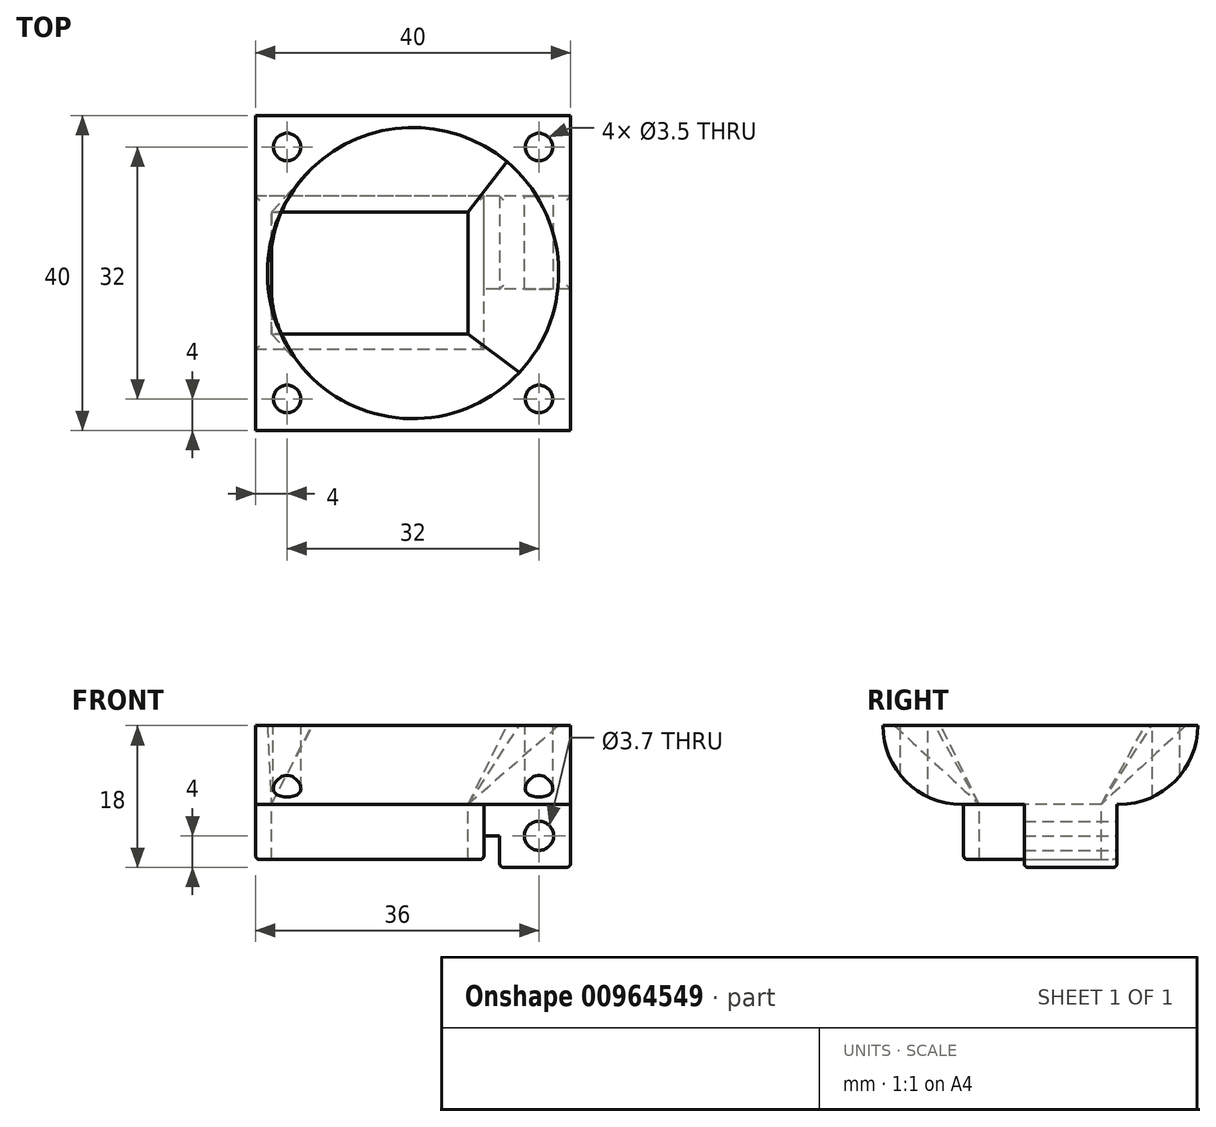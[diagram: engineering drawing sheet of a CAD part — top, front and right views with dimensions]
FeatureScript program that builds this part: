
annotation { "Feature Type Name" : "Feature", "Feature Type Description" : "" }
export const myFeature = defineFeature(function(context is Context, id is Id, definition is map)
    precondition{}
    {
        {
            var Q0;
            Q0=qCreatedBy(makeId("Top.planeOp"),FACE);
            var sketch = newSketch(context, id + "F0", { "sketchPlane" : qUnion([Q0])});
            skLineSegment(sketch, "E0.bottom", {"start": v(20, -9.75) * mm, "end": v(-20, -9.75) * mm});
            skLineSegment(sketch, "E0.top", {"start": v(20, 9.75) * mm, "end": v(-20, 9.75) * mm});
            skLineSegment(sketch, "E0.left", {"start": v(20, -9.75) * mm, "end": v(20, 9.75) * mm});
            skLineSegment(sketch, "E0.right", {"start": v(-20, -9.75) * mm, "end": v(-20, 9.75) * mm});
            skPoint(sketch, "E0.middle", {"position": v(0, 0) * mm});
            skLineSegment(sketch, "E1.bottom", {"start": v(20, -9.75) * mm, "end": v(9, -9.75) * mm});
            skLineSegment(sketch, "E1.top", {"start": v(20, -2.05) * mm, "end": v(9, -2.05) * mm});
            skLineSegment(sketch, "E1.left", {"start": v(20, -9.75) * mm, "end": v(20, -2.05) * mm});
            skLineSegment(sketch, "E1.right", {"start": v(9, -9.75) * mm, "end": v(9, -2.05) * mm});
            skSolve(sketch);
        }
        {
            var Q0;
            {var subQ1=sQuery(id+"F0.wireOp",EDGE,"E0.top");Q0=makeQuery(id+"F0.imprint","IMPRINT",FACE,{"disambiguationData":[TD([[makeQuery(id+"F0.imprint","IMPRINT",EDGE,{"derivedFrom":subQ1}),1.0]])]});}
            extrude(context, id + "F1", {"entities" : qUnion([Q0]), "oppositeDirection" : true, "depth" : 4 * mm, "offsetDistance" : 25 * mm});
        }
        {
            var Q0;
            Q0=makeQuery(id+"F1.opExtrude","CAP_FACE",FACE,{"disambiguationData":[OSD([sQuery(id+"F0.wireOp",EDGE,"E0.bottom"),sQuery(id+"F0.wireOp",EDGE,"E0.top"),sQuery(id+"F0.wireOp",EDGE,"E0.left"),sQuery(id+"F0.wireOp",EDGE,"E0.right"),sQuery(id+"F0.wireOp",EDGE,"E1.top"),sQuery(id+"F0.wireOp",EDGE,"E1.right")])],"isStart":false});
            var sketch = newSketch(context, id + "F2", { "sketchPlane" : qUnion([Q0])});
            skLineSegment(sketch, "E2.bottom", {"start": v(-20, 9.75) * mm, "end": v(9, 9.75) * mm});
            skLineSegment(sketch, "E2.top", {"start": v(-20, -9.75) * mm, "end": v(9, -9.75) * mm});
            skLineSegment(sketch, "E2.left", {"start": v(-20, 9.75) * mm, "end": v(-20, -9.75) * mm});
            skLineSegment(sketch, "E2.right", {"start": v(9, 9.75) * mm, "end": v(9, -9.75) * mm});
            skSolve(sketch);
        }
        {
            var Q0;
            Q0 = qSketchRegion(id + "F2", true);
            extrude(context, id + "F3", {"entities" : qUnion([Q0]), "operationType" : NewBodyOperationType.ADD, "depth" : 3 * mm, "offsetDistance" : 25 * mm});
        }
        {
            var Q0;
            Q0=makeQuery(id+"F1.opExtrude","CAP_FACE",FACE,{"disambiguationData":[OSD([sQuery(id+"F0.wireOp",EDGE,"E0.bottom"),sQuery(id+"F0.wireOp",EDGE,"E0.top"),sQuery(id+"F0.wireOp",EDGE,"E0.left"),sQuery(id+"F0.wireOp",EDGE,"E0.right"),sQuery(id+"F0.wireOp",EDGE,"E1.top"),sQuery(id+"F0.wireOp",EDGE,"E1.right")])],"isStart":false});
            var sketch = newSketch(context, id + "F4", { "sketchPlane" : qUnion([Q0])});
            skLineSegment(sketch, "E3.bottom", {"start": v(20, -9.75) * mm, "end": v(11, -9.75) * mm});
            skLineSegment(sketch, "E3.top", {"start": v(20, 2.05) * mm, "end": v(11, 2.05) * mm});
            skLineSegment(sketch, "E3.left", {"start": v(20, -9.75) * mm, "end": v(20, 2.05) * mm});
            skLineSegment(sketch, "E3.right", {"start": v(11, -9.75) * mm, "end": v(11, 2.05) * mm});
            skSolve(sketch);
        }
        {
            var Q0;
            Q0 = qSketchRegion(id + "F4", true);
            extrude(context, id + "F5", {"entities" : qUnion([Q0]), "operationType" : NewBodyOperationType.ADD, "depth" : 4 * mm, "offsetDistance" : 25 * mm});
        }
        {
            var Q0;
            Q0=makeQuery(id+"F5.boolean.opBoolean","MERGE",FACE,{"derivedFrom":[makeQuery(id+"F3.boolean.opBoolean","MERGE",FACE,{"derivedFrom":[makeQuery(id+"F1.opExtrude","SWEPT_FACE",FACE,{"disambiguationData":[OSD([sQuery(id+"F0.wireOp",EDGE,"E0.top")])]}),makeQuery(id+"F3.opExtrude","SWEPT_FACE",FACE,{"disambiguationData":[OSD([sQuery(id+"F2.wireOp",EDGE,"E2.top")])]})]}),makeQuery(id+"F5.opExtrude","SWEPT_FACE",FACE,{"disambiguationData":[OSD([sQuery(id+"F4.wireOp",EDGE,"E3.bottom")])]})]});
            var sketch = newSketch(context, id + "F6", { "sketchPlane" : qUnion([Q0])});
            skCircle(sketch, "E4", {"center": v(-16, -4) * mm, "radius": 1.85 * mm});
            skSolve(sketch);
        }
        {
            var Q0;
            Q0 = qSketchRegion(id + "F6", true);
            extrude(context, id + "F7", {"entities" : qUnion([Q0]), "operationType" : NewBodyOperationType.REMOVE, "endBound" : BoundingType.THROUGH_ALL, "oppositeDirection" : true, "depth" : 25 * mm, "offsetDistance" : 25 * mm});
        }
        {
            var Q0;
            Q0=makeQuery(id+"F1.opExtrude","CAP_FACE",FACE,{"disambiguationData":[OSD([sQuery(id+"F0.wireOp",EDGE,"E0.bottom"),sQuery(id+"F0.wireOp",EDGE,"E0.top"),sQuery(id+"F0.wireOp",EDGE,"E0.left"),sQuery(id+"F0.wireOp",EDGE,"E0.right"),sQuery(id+"F0.wireOp",EDGE,"E1.top"),sQuery(id+"F0.wireOp",EDGE,"E1.right")])],"isStart":true});
            var sketch = newSketch(context, id + "F8", { "sketchPlane" : qUnion([Q0])});
            skLineSegment(sketch, "E5.bottom", {"start": v(-18, 7.75) * mm, "end": v(7, 7.75) * mm});
            skLineSegment(sketch, "E5.top", {"start": v(-18, -7.75) * mm, "end": v(7, -7.75) * mm});
            skLineSegment(sketch, "E5.left", {"start": v(-18, 7.75) * mm, "end": v(-18, -7.75) * mm});
            skLineSegment(sketch, "E5.right", {"start": v(7, 7.75) * mm, "end": v(7, -7.75) * mm});
            skSolve(sketch);
        }
        {
            var Q0;
            Q0 = qSketchRegion(id + "F8", true);
            extrude(context, id + "F9", {"entities" : qUnion([Q0]), "operationType" : NewBodyOperationType.REMOVE, "endBound" : BoundingType.THROUGH_ALL, "oppositeDirection" : true, "depth" : 25 * mm, "offsetDistance" : 25 * mm});
        }
        {
            var Q0;
            Q0=makeQuery(id+"F1.opExtrude","CAP_FACE",FACE,{"disambiguationData":[OSD([sQuery(id+"F0.wireOp",EDGE,"E0.bottom"),sQuery(id+"F0.wireOp",EDGE,"E0.top"),sQuery(id+"F0.wireOp",EDGE,"E0.left"),sQuery(id+"F0.wireOp",EDGE,"E0.right"),sQuery(id+"F0.wireOp",EDGE,"E1.top"),sQuery(id+"F0.wireOp",EDGE,"E1.right")])],"isStart":true});
            var sketch = newSketch(context, id + "F10", { "sketchPlane" : qUnion([Q0])});
            skLineSegment(sketch, "E6.bottom", {"start": v(20, -20) * mm, "end": v(-20, -20) * mm});
            skLineSegment(sketch, "E6.top", {"start": v(20, 20) * mm, "end": v(-20, 20) * mm});
            skLineSegment(sketch, "E6.left", {"start": v(20, -20) * mm, "end": v(20, 20) * mm});
            skLineSegment(sketch, "E6.right", {"start": v(-20, -20) * mm, "end": v(-20, 20) * mm});
            skPoint(sketch, "E6.middle", {"position": v(0, 0) * mm});
            skSolve(sketch);
        }
        {
            var Q0;
            Q0 = qSketchRegion(id + "F10", true);
            extrude(context, id + "F11", {"entities" : qUnion([Q0]), "operationType" : NewBodyOperationType.ADD, "depth" : 10 * mm, "offsetDistance" : 25 * mm});
        }
        {
            var Q0;
            Q0=makeQuery(id+"F11.opExtrude","CAP_FACE",FACE,{"disambiguationData":[OSD([sQuery(id+"F10.wireOp",EDGE,"E6.bottom"),sQuery(id+"F10.wireOp",EDGE,"E6.top"),sQuery(id+"F10.wireOp",EDGE,"E6.left"),sQuery(id+"F10.wireOp",EDGE,"E6.right")])],"isStart":false});
            var sketch = newSketch(context, id + "F12", { "sketchPlane" : qUnion([Q0])});
            skArc(sketch, "E7", {"start": v(-12.84, 13.32) * mm, "mid": v(-18.5, -0.07) * mm, "end": v(-12.74, -13.41) * mm});
            skArc(sketch, "E8", {"start": v(11.92, 14.15) * mm, "mid": v(-0.62, 18.49) * mm, "end": v(-12.84, 13.32) * mm});
            skArc(sketch, "E9", {"start": v(13.5, -12.65) * mm, "mid": v(18.47, 1.1) * mm, "end": v(11.92, 14.15) * mm});
            skArc(sketch, "E10", {"start": v(-12.74, -13.41) * mm, "mid": v(0.54, -18.5) * mm, "end": v(13.5, -12.65) * mm});
            skSolve(sketch);
        }
        {
            var Q1;
            Q1 = qSketchRegion(id + "F8", true);
            var Q2;
            Q2=makeQuery(id+"F12.imprint","IMPRINT",FACE,{"disambiguationData":[TD([[makeQuery(id+"F12.imprint","IMPRINT",EDGE,{"derivedFrom":sQuery(id+"F12.wireOp",EDGE,"E7")}),1.0]])]});
            loft(context, id + "F13", {"operationType" : NewBodyOperationType.REMOVE, "sheetProfilesArray" : [{ "sheetProfileEntities" : qUnion([Q1]) }, { "sheetProfileEntities" : qUnion([Q2]) }]});
        }
        {
            var Q0;
            Q0=makeQuery(id+"F11.opExtrude","CAP_EDGE",EDGE,{"disambiguationData":[OSD([sQuery(id+"F10.wireOp",EDGE,"E6.bottom")])],"isStart":true});
            var Q1;
            Q1=makeQuery(id+"F11.opExtrude","CAP_EDGE",EDGE,{"disambiguationData":[OSD([sQuery(id+"F10.wireOp",EDGE,"E6.top")])],"isStart":true});
            fillet(context, id + "F14", {"entities" : qUnion([Q0, Q1]), "radius" : 10 * mm, "rho" : 0, "defaultsChanged" : false, "vertexSettings" : [], "crossSection" : FilletCrossSection.CONIC, "allowEdgeOverflow" : false});
        }
        {
            var Q0;
            Q0=makeQuery(id+"F11.opExtrude","CAP_FACE",FACE,{"disambiguationData":[OSD([sQuery(id+"F10.wireOp",EDGE,"E6.bottom"),sQuery(id+"F10.wireOp",EDGE,"E6.top"),sQuery(id+"F10.wireOp",EDGE,"E6.left"),sQuery(id+"F10.wireOp",EDGE,"E6.right")])],"isStart":false});
            var sketch = newSketch(context, id + "F15", { "sketchPlane" : qUnion([Q0])});
            skCircle(sketch, "E11", {"center": v(-16, 16) * mm, "radius": 1.75 * mm});
            skCircle(sketch, "E12", {"center": v(16, 16) * mm, "radius": 1.75 * mm});
            skCircle(sketch, "E13", {"center": v(16, -16) * mm, "radius": 1.75 * mm});
            skCircle(sketch, "E14", {"center": v(-16, -16) * mm, "radius": 1.75 * mm});
            skSolve(sketch);
        }
        {
            var Q0;
            Q0 = qSketchRegion(id + "F15", true);
            extrude(context, id + "F16", {"entities" : qUnion([Q0]), "operationType" : NewBodyOperationType.REMOVE, "endBound" : BoundingType.THROUGH_ALL, "oppositeDirection" : true, "depth" : 25 * mm, "offsetDistance" : 25 * mm});
        }
        {
            var Q0;
            Q0=makeQuery(id+"F3.opExtrude","CAP_EDGE",EDGE,{"disambiguationData":[OSD([sQuery(id+"F2.wireOp",EDGE,"E2.top")])],"isStart":false});
            var Q1;
            Q1=makeQuery(id+"F3.opExtrude","CAP_EDGE",EDGE,{"disambiguationData":[OSD([sQuery(id+"F2.wireOp",EDGE,"E2.left")])],"isStart":false});
            var Q2;
            Q2=makeQuery(id+"F3.opExtrude","CAP_EDGE",EDGE,{"disambiguationData":[OSD([sQuery(id+"F2.wireOp",EDGE,"E2.bottom")])],"isStart":false});
            var Q3;
            Q3=makeQuery(id+"F3.opExtrude","CAP_EDGE",EDGE,{"disambiguationData":[OSD([sQuery(id+"F2.wireOp",EDGE,"E2.right")])],"isStart":false});
            var Q4;
            Q4=makeQuery(id+"F5.opExtrude","CAP_EDGE",EDGE,{"disambiguationData":[OSD([sQuery(id+"F4.wireOp",EDGE,"E3.top")])],"isStart":false});
            var Q5;
            Q5=makeQuery(id+"F5.opExtrude","CAP_EDGE",EDGE,{"disambiguationData":[OSD([sQuery(id+"F4.wireOp",EDGE,"E3.right")])],"isStart":false});
            var Q6;
            Q6=makeQuery(id+"F5.opExtrude","CAP_EDGE",EDGE,{"disambiguationData":[OSD([sQuery(id+"F4.wireOp",EDGE,"E3.bottom")])],"isStart":false});
            var Q7;
            Q7=makeQuery(id+"F5.opExtrude","CAP_EDGE",EDGE,{"disambiguationData":[OSD([sQuery(id+"F4.wireOp",EDGE,"E3.left")])],"isStart":false});
            fillet(context, id + "F17", {"entities" : qUnion([Q0, Q1, Q2, Q3, Q4, Q5, Q6, Q7]), "radius" : .5 * mm, "tangentPropagation" : true, "defaultsChanged" : false, "vertexSettings" : [], "allowEdgeOverflow" : false});
        }
    });
